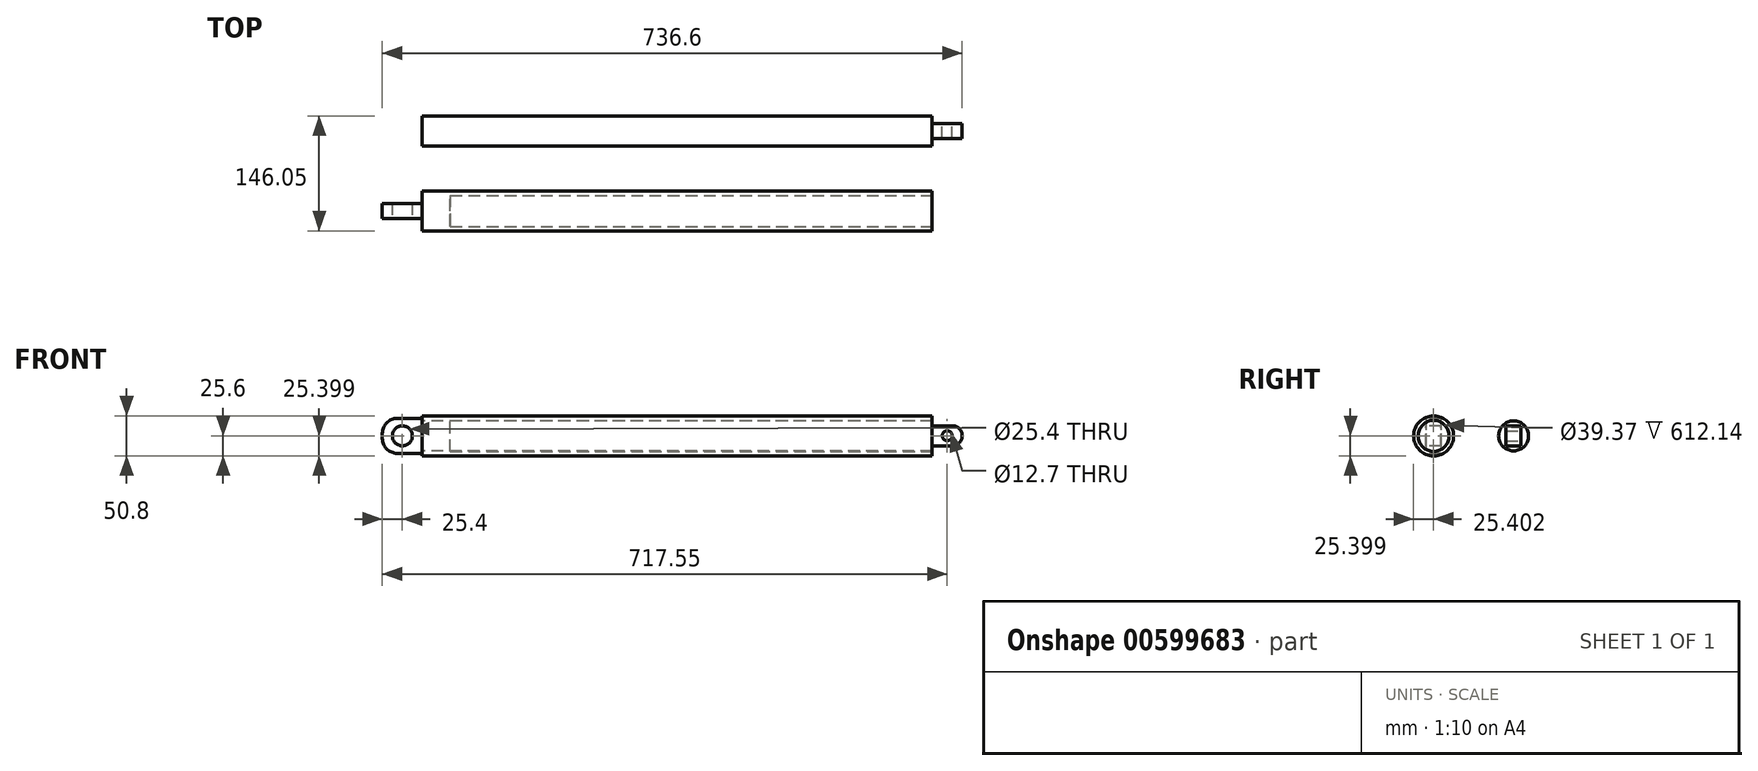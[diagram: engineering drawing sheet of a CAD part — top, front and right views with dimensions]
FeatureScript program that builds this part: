
annotation { "Feature Type Name" : "Feature", "Feature Type Description" : "" }
export const myFeature = defineFeature(function(context is Context, id is Id, definition is map)
    precondition{}
    {
        {
            var Q0;
            Q0=qCreatedBy(makeId("Right.planeOp"),FACE);
            var sketch = newSketch(context, id + "F0", { "sketchPlane" : qUnion([Q0])});
            skCircle(sketch, "E0", {"center": v(-47.14, 18.65) * mm, "radius": 25.4 * mm});
            skCircle(sketch, "E1", {"center": v(54.46, 18.65) * mm, "radius": 19.05 * mm});
            skSolve(sketch);
        }
        {
            var Q0;
            Q0=makeQuery(id+"F0.imprint","IMPRINT",FACE,{"disambiguationData":[TD([[makeQuery(id+"F0.imprint","IMPRINT",EDGE,{"derivedFrom":sQuery(id+"F0.wireOp",EDGE,"E0")}),1.0]])]});
            var Q1;
            Q1=makeQuery(id+"F0.imprint","IMPRINT",FACE,{"disambiguationData":[TD([[makeQuery(id+"F0.imprint","IMPRINT",EDGE,{"derivedFrom":sQuery(id+"F0.wireOp",EDGE,"E1")}),1.0]])]});
            extrude(context, id + "F1", {"entities" : qUnion([Q0, Q1]), "depth" : 647.7 * mm, "offsetDistance" : 25.4 * mm});
        }
        {
            var Q0;
            Q0=makeQuery(id+"F1.opExtrude","CAP_FACE",FACE,{"disambiguationData":[OSD([sQuery(id+"F0.wireOp",EDGE,"E0")])],"isStart":false});
            var sketch = newSketch(context, id + "F2", { "sketchPlane" : qUnion([Q0])});
            skCircle(sketch, "E2", {"center": v(-47.14, 18.65) * mm, "radius": 19.69 * mm});
            skSolve(sketch);
        }
        {
            var Q0;
            Q0=makeQuery(id+"F2.imprint","IMPRINT",FACE,{"disambiguationData":[TD([[makeQuery(id+"F2.imprint","IMPRINT",EDGE,{"derivedFrom":sQuery(id+"F2.wireOp",EDGE,"E2")}),1.0]])]});
            extrude(context, id + "F3", {"entities" : qUnion([Q0]), "operationType" : NewBodyOperationType.REMOVE, "oppositeDirection" : true, "depth" : 612.14 * mm, "offsetDistance" : 25.4 * mm});
        }
        {
            var Q0;
            Q0=makeQuery(id+"F1.opExtrude","CAP_FACE",FACE,{"disambiguationData":[OSD([sQuery(id+"F0.wireOp",EDGE,"E0")])],"isStart":true});
            var sketch = newSketch(context, id + "F4", { "sketchPlane" : qUnion([Q0])});
            skLineSegment(sketch, "E3.bottom", {"start": v(37.61, 40.87) * mm, "end": v(56.66, 40.87) * mm});
            skLineSegment(sketch, "E3.top", {"start": v(37.61, -3.58) * mm, "end": v(56.66, -3.58) * mm});
            skLineSegment(sketch, "E3.left", {"start": v(37.61, 40.87) * mm, "end": v(37.61, -3.58) * mm});
            skLineSegment(sketch, "E3.right", {"start": v(56.66, 40.87) * mm, "end": v(56.66, -3.58) * mm});
            skSolve(sketch);
        }
        {
            var Q0;
            {var subQ0=sQuery(id+"F4.wireOp",EDGE,"E3.left");var subQ1=makeQuery(id+"F3.boolean.opBoolean","INTERSECT",EDGE,{"derivedFrom":[makeQuery(id+"F1.opExtrude","CAP_FACE",FACE,{"disambiguationData":[OSD([sQuery(id+"F0.wireOp",EDGE,"E0")])],"isStart":true}),makeQuery(id+"F3.opExtrude","SWEPT_FACE",FACE,{"disambiguationData":[OSD([sQuery(id+"F2.wireOp",EDGE,"E2")])]})]});var subQ2=makeQuery(id+"F4.imprint","INTERSECT",VERTEX,{"disambiguationData":[OD(0.0)],"derivedFrom":[subQ1,subQ0]});Q0=makeQuery(id+"F4.imprint","IMPRINT",FACE,{"disambiguationData":[TD([[makeQuery(id+"F4.imprint","IMPRINT",EDGE,{"disambiguationData":[TD([[subQ2,-1.0]])],"derivedFrom":subQ0}),1.0]])]});}
            var Q1;
            {var subQ0=sQuery(id+"F4.wireOp",EDGE,"E3.bottom");Q1=makeQuery(id+"F4.imprint","IMPRINT",FACE,{"disambiguationData":[TD([[makeQuery(id+"F4.imprint","IMPRINT",EDGE,{"derivedFrom":subQ0}),-1.0]])]});}
            var Q2;
            {var subQ0=sQuery(id+"F4.wireOp",EDGE,"E3.top");Q2=makeQuery(id+"F4.imprint","IMPRINT",FACE,{"disambiguationData":[TD([[makeQuery(id+"F4.imprint","IMPRINT",EDGE,{"derivedFrom":subQ0}),1.0]])]});}
            extrude(context, id + "F5", {"entities" : qUnion([Q0, Q1, Q2]), "operationType" : NewBodyOperationType.ADD, "depth" : 50.8 * mm, "offsetDistance" : 25.4 * mm});
        }
        {
            var Q0;
            Q0=makeQuery(id+"F5.opExtrude","SWEPT_FACE",FACE,{"disambiguationData":[OSD([sQuery(id+"F4.wireOp",EDGE,"E3.right")])]});
            var sketch = newSketch(context, id + "F6", { "sketchPlane" : qUnion([Q0])});
            skCircle(sketch, "E4", {"center": v(-25.4, 18.65) * mm, "radius": 12.7 * mm});
            skPoint(sketch, "E4.centerSnap0", {"position": v(-50.8, 18.65) * mm});
            skPoint(sketch, "E4.centerSnap1", {"position": v(-25.4, 40.87) * mm});
            skSolve(sketch);
        }
        {
            var Q0;
            Q0=makeQuery(id+"F6.imprint","IMPRINT",FACE,{"disambiguationData":[TD([[makeQuery(id+"F6.imprint","IMPRINT",EDGE,{"derivedFrom":sQuery(id+"F6.wireOp",EDGE,"E4")}),1.0]])]});
            extrude(context, id + "F7", {"entities" : qUnion([Q0]), "operationType" : NewBodyOperationType.REMOVE, "endBound" : BoundingType.THROUGH_ALL, "oppositeDirection" : true, "depth" : 25.4 * mm, "offsetDistance" : 25.4 * mm});
        }
        {
            var Q0;
            Q0=makeQuery(id+"F5.opExtrude","CAP_EDGE",EDGE,{"disambiguationData":[OSD([sQuery(id+"F4.wireOp",EDGE,"E3.bottom")])],"isStart":false});
            var Q1;
            Q1=makeQuery(id+"F5.opExtrude","CAP_EDGE",EDGE,{"disambiguationData":[OSD([sQuery(id+"F4.wireOp",EDGE,"E3.top")])],"isStart":false});
            fillet(context, id + "F8", {"entities" : qUnion([Q0, Q1]), "radius" : 19.05 * mm, "tangentPropagation" : true, "allowEdgeOverflow" : false});
        }
        {
            var Q0;
            Q0=makeQuery(id+"F1.opExtrude","CAP_FACE",FACE,{"disambiguationData":[OSD([sQuery(id+"F0.wireOp",EDGE,"E1")])],"isStart":false});
            var sketch = newSketch(context, id + "F9", { "sketchPlane" : qUnion([Q0])});
            skLineSegment(sketch, "E5.bottom", {"start": v(44.94, 31.55) * mm, "end": v(63.99, 31.55) * mm});
            skLineSegment(sketch, "E5.top", {"start": v(44.94, 6.15) * mm, "end": v(63.99, 6.15) * mm});
            skLineSegment(sketch, "E5.left", {"start": v(44.94, 31.55) * mm, "end": v(44.94, 6.15) * mm});
            skLineSegment(sketch, "E5.right", {"start": v(63.99, 31.55) * mm, "end": v(63.99, 6.15) * mm});
            skLineSegment(sketch, "E6", {"start": v(54.46, 31.55) * mm, "end": v(54.46, 37.7) * mm, "construction": true});
            skLineSegment(sketch, "E7", {"start": v(54.46, 6.15) * mm, "end": v(54.46, 0) * mm, "construction": true});
            skLineSegment(sketch, "E8", {"start": v(54.46, 0) * mm, "end": v(54.41, -0.57) * mm, "construction": true});
            skLineSegment(sketch, "E9", {"start": v(44.94, 18.85) * mm, "end": v(35.41, 18.85) * mm, "construction": true});
            skLineSegment(sketch, "E10", {"start": v(63.99, 18.85) * mm, "end": v(73.51, 18.85) * mm, "construction": true});
            skSolve(sketch);
        }
        {
            var Q0;
            Q0=makeQuery(id+"F9.imprint","IMPRINT",FACE,{"disambiguationData":[TD([[makeQuery(id+"F9.imprint","IMPRINT",EDGE,{"derivedFrom":sQuery(id+"F9.wireOp",EDGE,"E5.bottom")}),-1.0]])]});
            extrude(context, id + "F10", {"entities" : qUnion([Q0]), "operationType" : NewBodyOperationType.ADD, "depth" : 38.1 * mm, "offsetDistance" : 25.4 * mm});
        }
        {
            var Q0;
            Q0=makeQuery(id+"F10.opExtrude","SWEPT_FACE",FACE,{"disambiguationData":[OSD([sQuery(id+"F9.wireOp",EDGE,"E5.right")])]});
            var sketch = newSketch(context, id + "F11", { "sketchPlane" : qUnion([Q0])});
            skCircle(sketch, "E11", {"center": v(-666.75, 18.85) * mm, "radius": 6.35 * mm});
            skPoint(sketch, "E11.centerSnap0", {"position": v(-685.8, 18.85) * mm});
            skPoint(sketch, "E11.centerSnap1", {"position": v(-666.75, 31.55) * mm});
            skSolve(sketch);
        }
        {
            var Q0;
            Q0=makeQuery(id+"F11.imprint","IMPRINT",FACE,{"disambiguationData":[TD([[makeQuery(id+"F11.imprint","IMPRINT",EDGE,{"derivedFrom":sQuery(id+"F11.wireOp",EDGE,"E11")}),1.0]])]});
            extrude(context, id + "F12", {"entities" : qUnion([Q0]), "operationType" : NewBodyOperationType.REMOVE, "endBound" : BoundingType.THROUGH_ALL, "oppositeDirection" : true, "depth" : 25.4 * mm, "offsetDistance" : 25.4 * mm});
        }
        {
            var Q0;
            Q0=makeQuery(id+"F10.opExtrude","CAP_EDGE",EDGE,{"disambiguationData":[OSD([sQuery(id+"F9.wireOp",EDGE,"E5.bottom")])],"isStart":false});
            var Q1;
            Q1=makeQuery(id+"F10.opExtrude","CAP_EDGE",EDGE,{"disambiguationData":[OSD([sQuery(id+"F9.wireOp",EDGE,"E5.top")])],"isStart":false});
            fillet(context, id + "F13", {"entities" : qUnion([Q0, Q1]), "radius" : 12.7 * mm, "tangentPropagation" : true, "allowEdgeOverflow" : false});
        }
    });
